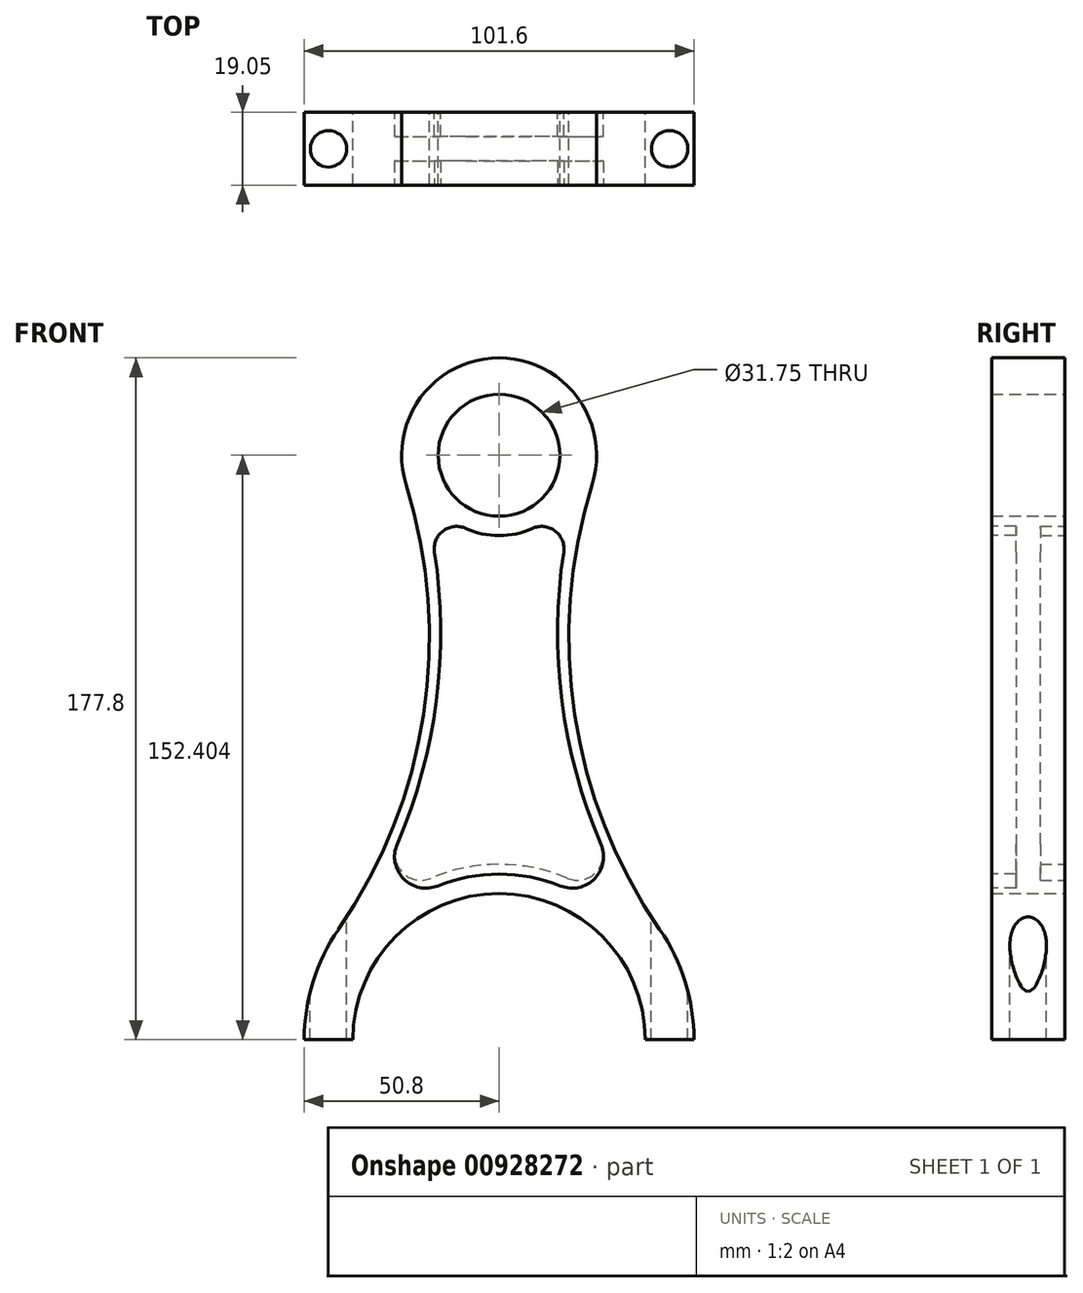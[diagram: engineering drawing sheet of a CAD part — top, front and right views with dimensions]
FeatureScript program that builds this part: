
annotation { "Feature Type Name" : "Feature", "Feature Type Description" : "" }
export const myFeature = defineFeature(function(context is Context, id is Id, definition is map)
    precondition{}
    {
        {
            var Q0;
            Q0=qCreatedBy(makeId("Front.planeOp"),FACE);
            var sketch = newSketch(context, id + "F0", { "sketchPlane" : qUnion([Q0])});
            skArc(sketch, "E0", {"start": v(-41.84, -22.14) * mm, "mid": v(-19.7, 33.86) * mm, "end": v(-24.25, 93.9) * mm});
            skArc(sketch, "E1", {"start": v(24.25, 93.9) * mm, "mid": v(19.7, 33.86) * mm, "end": v(41.84, -22.14) * mm});
            skArc(sketch, "E2", {"start": v(24.25, 93.9) * mm, "mid": v(0, 126.85) * mm, "end": v(-24.25, 93.9) * mm});
            skArc(sketch, "E3", {"start": v(-41.84, -22.14) * mm, "mid": v(0, -101.75) * mm, "end": v(41.84, -22.14) * mm});
            skCircle(sketch, "E4", {"center": v(0, -50.95) * mm, "radius": 38.1 * mm});
            skCircle(sketch, "E5", {"center": v(0, 101.45) * mm, "radius": 15.88 * mm});
            skLineSegment(sketch, "E6", {"start": v(0, -50.95) * mm, "end": v(127, -50.95) * mm});
            skLineSegment(sketch, "E7", {"start": v(0, -50.95) * mm, "end": v(-127, -50.95) * mm});
            skLineSegment(sketch, "E8", {"start": v(-127, -50.95) * mm, "end": v(-127, -104.92) * mm});
            skLineSegment(sketch, "E9", {"start": v(-127, -104.92) * mm, "end": v(127, -104.92) * mm});
            skLineSegment(sketch, "E10", {"start": v(127, -104.92) * mm, "end": v(127, -50.95) * mm});
            skSolve(sketch);
        }
        {
            var Q0;
            Q0=makeQuery(id+"F0.imprint","IMPRINT",FACE,{"disambiguationData":[TD([[makeQuery(id+"F0.imprint","IMPRINT",EDGE,{"derivedFrom":sQuery(id+"F0.wireOp",EDGE,"E0")}),-1.0]])]});
            extrude(context, id + "F1", {"entities" : qUnion([Q0]), "depth" : 19.05 * mm, "offsetDistance" : 25.4 * mm});
        }
        {
            var Q0;
            Q0=qCreatedBy(makeId("Top.planeOp"),FACE);
            var sketch = newSketch(context, id + "F2", { "sketchPlane" : qUnion([Q0])});
            skCircle(sketch, "E11", {"center": v(-44.45, -9.53) * mm, "radius": 4.76 * mm});
            skCircle(sketch, "E12", {"center": v(44.45, -9.53) * mm, "radius": 4.76 * mm});
            skSolve(sketch);
        }
        {
            var Q0;
            Q0=makeQuery(id+"F2.imprint","IMPRINT",FACE,{"disambiguationData":[TD([[makeQuery(id+"F2.imprint","IMPRINT",EDGE,{"derivedFrom":sQuery(id+"F2.wireOp",EDGE,"E11")}),1.0]])]});
            var Q1;
            Q1=makeQuery(id+"F2.imprint","IMPRINT",FACE,{"disambiguationData":[TD([[makeQuery(id+"F2.imprint","IMPRINT",EDGE,{"derivedFrom":sQuery(id+"F2.wireOp",EDGE,"E12")}),1.0]])]});
            extrude(context, id + "F3", {"entities" : qUnion([Q0, Q1]), "operationType" : NewBodyOperationType.REMOVE, "oppositeDirection" : true, "depth" : 53.97 * mm, "offsetDistance" : 25.4 * mm});
        }
        {
            var Q0;
            Q0=qCreatedBy(makeId("Front.planeOp"),FACE);
            var sketch = newSketch(context, id + "F4", { "sketchPlane" : qUnion([Q0])});
            skArc(sketch, "E13", {"start": v(-26.58, 0) * mm, "mid": v(-16.37, 37.42) * mm, "end": v(-16.84, 76.2) * mm});
            skArc(sketch, "E14", {"start": v(16.84, 76.2) * mm, "mid": v(16.37, 37.42) * mm, "end": v(26.58, 0) * mm});
            skArc(sketch, "E15", {"start": v(17.8, -8.83) * mm, "mid": v(25.17, -7.38) * mm, "end": v(26.58, 0) * mm});
            skArc(sketch, "E16", {"start": v(-8.67, 82.38) * mm, "mid": v(-14.6, 81.72) * mm, "end": v(-16.84, 76.2) * mm});
            skArc(sketch, "E17", {"start": v(17.8, -8.83) * mm, "mid": v(0, -5.23) * mm, "end": v(-17.8, -8.83) * mm});
            skPoint(sketch, "E18.startSnap0", {"position": v(0, -5.23) * mm});
            skArc(sketch, "E19", {"start": v(-8.67, 82.38) * mm, "mid": v(0, 80.5) * mm, "end": v(8.67, 82.38) * mm});
            skArc(sketch, "E20", {"start": v(16.84, 76.2) * mm, "mid": v(14.6, 81.72) * mm, "end": v(8.67, 82.38) * mm});
            skArc(sketch, "E21", {"start": v(-26.58, 0) * mm, "mid": v(-25.17, -7.38) * mm, "end": v(-17.8, -8.83) * mm});
            skSolve(sketch);
        }
        {
            var Q0;
            Q0=makeQuery(id+"F4.imprint","IMPRINT",FACE,{"disambiguationData":[TD([[makeQuery(id+"F4.imprint","IMPRINT",EDGE,{"derivedFrom":sQuery(id+"F4.wireOp",EDGE,"E13")}),-1.0]])]});
            extrude(context, id + "F5", {"entities" : qUnion([Q0]), "operationType" : NewBodyOperationType.REMOVE, "depth" : 6.35 * mm, "offsetDistance" : 25.4 * mm});
        }
        {
            var Q0;
            Q0=makeQuery(id+"F1.opExtrude","CAP_FACE",FACE,{"disambiguationData":[OSD([sQuery(id+"F0.wireOp",EDGE,"E0"),sQuery(id+"F0.wireOp",EDGE,"E1"),sQuery(id+"F0.wireOp",EDGE,"E2"),sQuery(id+"F0.wireOp",EDGE,"E3"),sQuery(id+"F0.wireOp",EDGE,"E4"),sQuery(id+"F0.wireOp",EDGE,"E5"),sQuery(id+"F0.wireOp",EDGE,"E6"),sQuery(id+"F0.wireOp",EDGE,"E7")])],"isStart":false});
            var sketch = newSketch(context, id + "F6", { "sketchPlane" : qUnion([Q0])});
            skArc(sketch, "E22", {"start": v(-26.58, 0) * mm, "mid": v(-16.37, 37.42) * mm, "end": v(-16.84, 76.2) * mm});
            skArc(sketch, "E23", {"start": v(16.84, 76.2) * mm, "mid": v(16.37, 37.42) * mm, "end": v(26.58, 0) * mm});
            skArc(sketch, "E24", {"start": v(16.01, -10.84) * mm, "mid": v(24.92, -8.95) * mm, "end": v(26.58, 0) * mm});
            skArc(sketch, "E25", {"start": v(-26.58, 0) * mm, "mid": v(-24.92, -8.95) * mm, "end": v(-16.01, -10.84) * mm});
            skArc(sketch, "E26", {"start": v(-8.67, 82.38) * mm, "mid": v(-14.6, 81.72) * mm, "end": v(-16.84, 76.2) * mm});
            skArc(sketch, "E27", {"start": v(16.01, -10.84) * mm, "mid": v(0, -7.77) * mm, "end": v(-16.01, -10.84) * mm});
            skPoint(sketch, "E28.startSnap0", {"position": v(0, -7.77) * mm});
            skArc(sketch, "E29", {"start": v(-8.67, 82.38) * mm, "mid": v(0, 80.5) * mm, "end": v(8.67, 82.38) * mm});
            skArc(sketch, "E30", {"start": v(16.84, 76.2) * mm, "mid": v(14.6, 81.72) * mm, "end": v(8.67, 82.38) * mm});
            skSolve(sketch);
        }
        {
            var Q0;
            Q0=makeQuery(id+"F6.imprint","IMPRINT",FACE,{"disambiguationData":[TD([[makeQuery(id+"F6.imprint","IMPRINT",EDGE,{"derivedFrom":sQuery(id+"F6.wireOp",EDGE,"E22")}),-1.0]])]});
            extrude(context, id + "F7", {"entities" : qUnion([Q0]), "operationType" : NewBodyOperationType.REMOVE, "oppositeDirection" : true, "depth" : 6.35 * mm, "offsetDistance" : 25.4 * mm});
        }
    });
